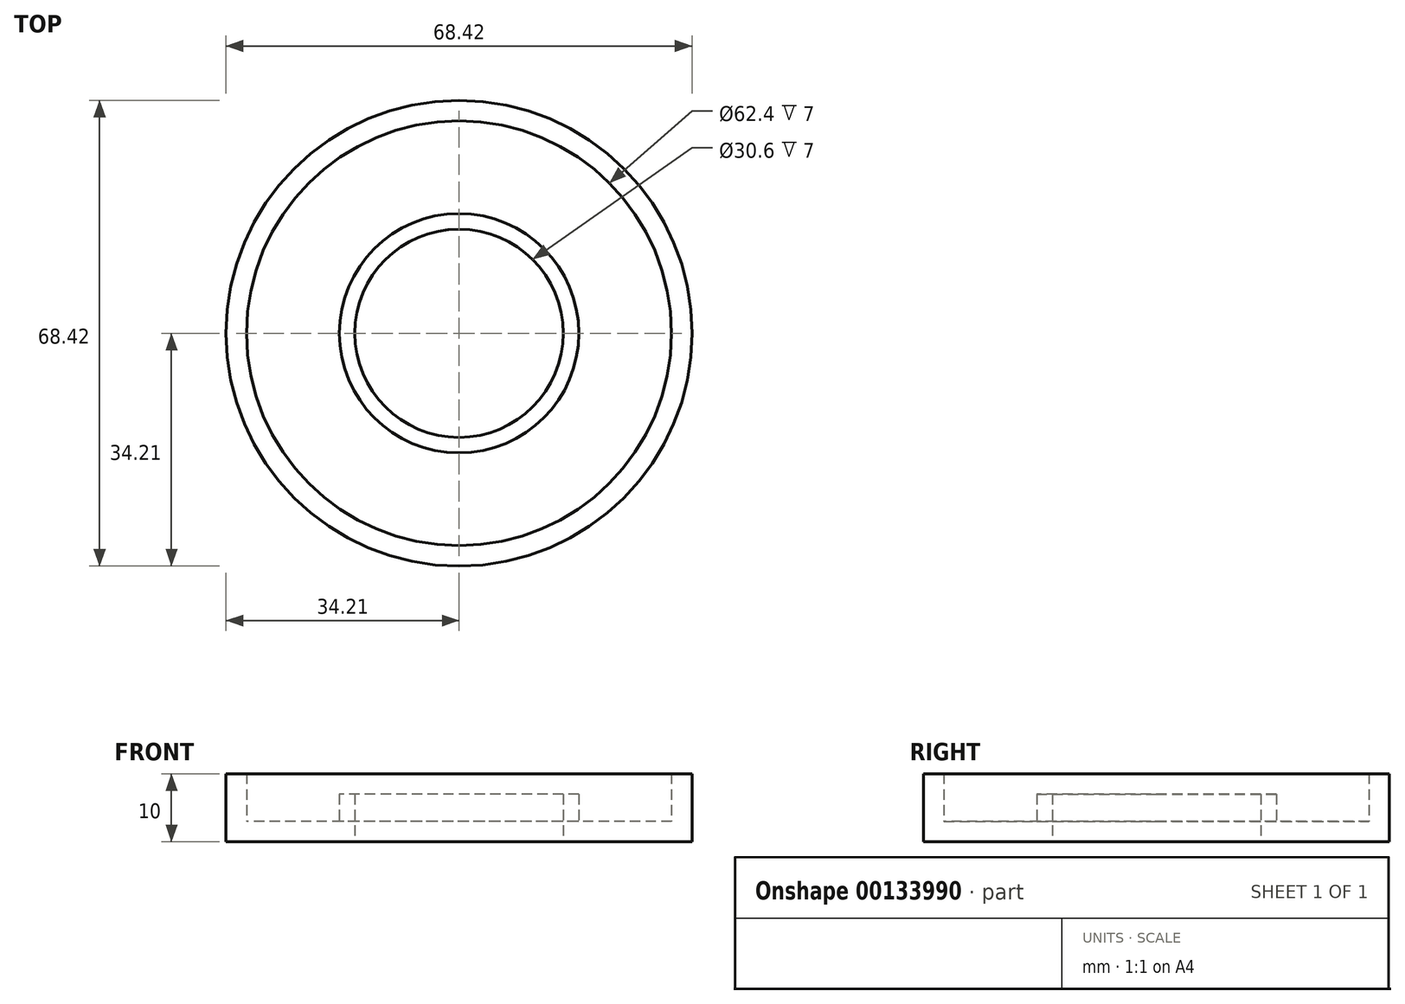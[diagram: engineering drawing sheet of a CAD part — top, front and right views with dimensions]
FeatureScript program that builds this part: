
annotation { "Feature Type Name" : "Feature", "Feature Type Description" : "" }
export const myFeature = defineFeature(function(context is Context, id is Id, definition is map)
    precondition{}
    {
        {
            var Q0;
            Q0=qCreatedBy(makeId("Top.planeOp"),FACE);
            var sketch = newSketch(context, id + "F0", { "sketchPlane" : qUnion([Q0])});
            skCircle(sketch, "E0", {"center": v(0, 0) * mm, "radius": 34.2 * mm});
            skCircle(sketch, "E1", {"center": v(0, 0) * mm, "radius": 16 * mm});
            skCircle(sketch, "E2", {"center": v(0, 0) * mm, "radius": 31.2 * mm});
            skSolve(sketch);
        }
        {
            var Q0;
            Q0=makeQuery(id+"F0.imprint","IMPRINT",FACE,{"disambiguationData":[TD([[makeQuery(id+"F0.imprint","IMPRINT",EDGE,{"derivedFrom":sQuery(id+"F0.wireOp",EDGE,"E0")}),1.0]])]});
            extrude(context, id + "F1", {"entities" : qUnion([Q0]), "depth" : 10 * mm});
        }
        {
            var Q0;
            Q0=qCreatedBy(makeId("Top.planeOp"),FACE);
            var sketch = newSketch(context, id + "F2", { "sketchPlane" : qUnion([Q0])});
            skCircle(sketch, "E3", {"center": v(0, 0) * mm, "radius": 33.65 * mm});
            skCircle(sketch, "E4", {"center": v(0, 0) * mm, "radius": 15.36 * mm});
            skSolve(sketch);
        }
        {
            var Q0;
            Q0=makeQuery(id+"F2.imprint","IMPRINT",FACE,{"disambiguationData":[TD([[makeQuery(id+"F2.imprint","IMPRINT",EDGE,{"derivedFrom":sQuery(id+"F2.wireOp",EDGE,"E3")}),1.0]])]});
            extrude(context, id + "F3", {"entities" : qUnion([Q0]), "operationType" : NewBodyOperationType.ADD, "depth" : 3 * mm});
        }
        {
            var Q0;
            Q0=qCreatedBy(makeId("Top.planeOp"),FACE);
            var sketch = newSketch(context, id + "F4", { "sketchPlane" : qUnion([Q0])});
            skCircle(sketch, "E5", {"center": v(0, 0) * mm, "radius": 15.3 * mm});
            skCircle(sketch, "E6", {"center": v(0, 0) * mm, "radius": 17.58 * mm});
            skSolve(sketch);
        }
        {
            var Q0;
            Q0=makeQuery(id+"F4.imprint","IMPRINT",FACE,{"disambiguationData":[TD([[makeQuery(id+"F4.imprint","IMPRINT",EDGE,{"derivedFrom":sQuery(id+"F4.wireOp",EDGE,"E5")}),-1.0]])]});
            extrude(context, id + "F5", {"entities" : qUnion([Q0]), "operationType" : NewBodyOperationType.ADD, "depth" : 7 * mm});
        }
    });
